# Revit family: WindowShade_RolleaseAcmeda_ContractSeries1_4inFascia_R20
name_source: partatom
category: Specialty Equipment
units: mm (PartAtom-declared; Revit-internal decimal feet)

## family parameters
Always vertical = Yes
Cut with Voids When Loaded = No
Host = Wall
Part Type = Normal
Room Calculation Point = No
Round Connector Dimension = Use Diameter
Shared = No

## types (3) — shared parameters
Chain Length = 6' - 9 19/32"
Default Elevation = 10' - 0"
Description = RAC Series 1 - 4" Fascia System
Drop Bar Internal Hem = Yes
Drop Bar Silent Weight = No
Header Finish = RA - FINISH - WHITE
Input Bracket Width = 5' - 0"
Input Shade Drop = 8' - 0"
Manufacturer = Rollease Acmeda
Model = RA - Contract Series
Shade Drop Calc = 8' - 0"
Shade Fabric = RA - FABRIC - AMBIENT REVIEW
Shade Width Calc = 5' - 0"
URL = https://www.rolleaseacmedacontract.com
Weight Bar = RA - FINISH - WHITE

## per-type parameters (varying)
| type | Drive Manual LH (Select One) | Drive Manual Left Calc | Drive Manual RH (Select One) | Drive Manual Right Calc | Drive Motorized (Select One) | Drive Motorized Calc |
| 5'W x 8'Drop - Manual Left - White | Yes | Yes | No | No | No | No |
| 5'W x 8'Drop - Manual Right - White | No | No | Yes | Yes | No | No |
| 5'W x 8'Drop - Motorized - White | No | No | No | No | Yes | Yes |

## geometry (parser evidence)
native form markers: Sweep x19
no freeform markers — native parametric forms only
